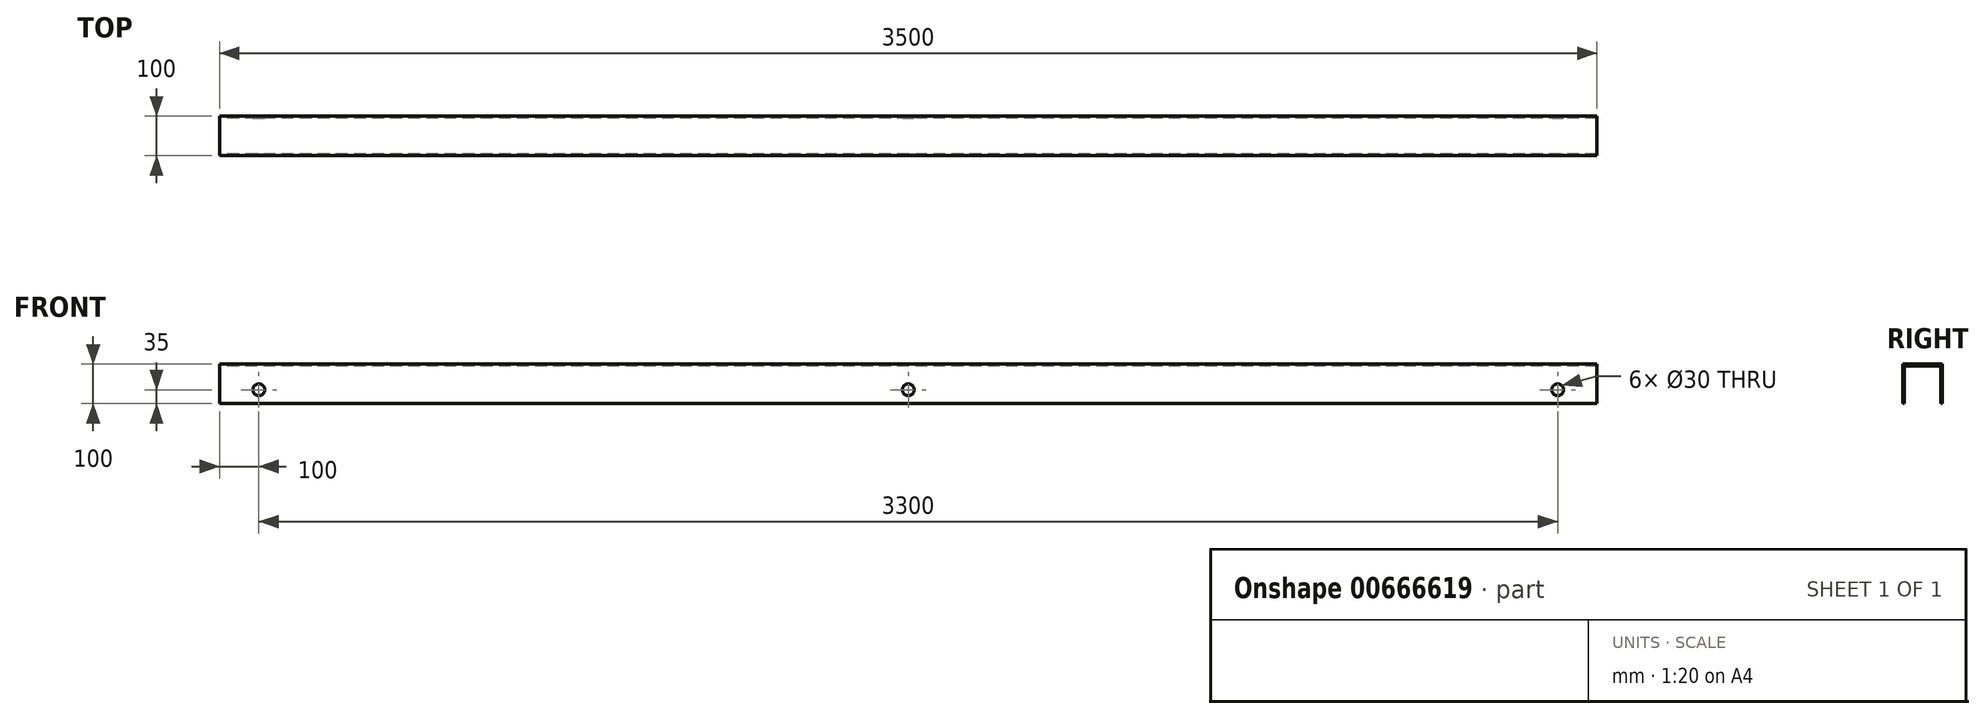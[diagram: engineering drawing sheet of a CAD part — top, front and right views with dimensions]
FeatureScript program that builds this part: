
annotation { "Feature Type Name" : "Feature", "Feature Type Description" : "" }
export const myFeature = defineFeature(function(context is Context, id is Id, definition is map)
    precondition{}
    {
        {
            var Q0;
            Q0=qCreatedBy(makeId("Right.planeOp"),FACE);
            var sketch = newSketch(context, id + "F0", { "sketchPlane" : qUnion([Q0])});
            skLineSegment(sketch, "E0", {"start": v(-37.2, 0) * mm, "end": v(-37.2, 100) * mm});
            skLineSegment(sketch, "E1", {"start": v(-37.2, 100) * mm, "end": v(62.8, 100) * mm});
            skLineSegment(sketch, "E2", {"start": v(62.8, 100) * mm, "end": v(62.8, 0) * mm});
            skLineSegment(sketch, "E3", {"start": v(62.8, 0) * mm, "end": v(58.8, 0) * mm});
            skLineSegment(sketch, "E4", {"start": v(58.8, 0) * mm, "end": v(58.8, 96) * mm});
            skLineSegment(sketch, "E5", {"start": v(58.8, 96) * mm, "end": v(-33.2, 96) * mm});
            skLineSegment(sketch, "E6", {"start": v(-33.2, 96) * mm, "end": v(-33.2, 0) * mm});
            skLineSegment(sketch, "E7", {"start": v(-33.2, 0) * mm, "end": v(-37.2, 0) * mm});
            skSolve(sketch);
        }
        {
            var Q0;
            Q0=makeQuery(id+"F0.imprint","IMPRINT",FACE,{"disambiguationData":[TD([[makeQuery(id+"F0.imprint","IMPRINT",EDGE,{"derivedFrom":sQuery(id+"F0.wireOp",EDGE,"E0")}),-1.0]])]});
            extrude(context, id + "F1", {"entities" : qUnion([Q0]), "depth" : 3500 * mm, "offsetDistance" : 25 * mm});
        }
        {
            var Q0;
            Q0=makeQuery(id+"F1.opExtrude","SWEPT_FACE",FACE,{"disambiguationData":[OSD([sQuery(id+"F0.wireOp",EDGE,"E2")])]});
            var sketch = newSketch(context, id + "F2", { "sketchPlane" : qUnion([Q0])});
            skCircle(sketch, "E8", {"center": v(-3400, 35) * mm, "radius": 15 * mm});
            skCircle(sketch, "E9", {"center": v(-1750, 35) * mm, "radius": 15 * mm});
            skCircle(sketch, "E10", {"center": v(-100, 35) * mm, "radius": 15 * mm});
            skSolve(sketch);
        }
        {
            var Q0;
            Q0=makeQuery(id+"F2.imprint","IMPRINT",FACE,{"disambiguationData":[TD([[makeQuery(id+"F2.imprint","IMPRINT",EDGE,{"derivedFrom":sQuery(id+"F2.wireOp",EDGE,"E8")}),1.0]])]});
            var Q1;
            Q1=makeQuery(id+"F2.imprint","IMPRINT",FACE,{"disambiguationData":[TD([[makeQuery(id+"F2.imprint","IMPRINT",EDGE,{"derivedFrom":sQuery(id+"F2.wireOp",EDGE,"E9")}),1.0]])]});
            var Q2;
            Q2=makeQuery(id+"F2.imprint","IMPRINT",FACE,{"disambiguationData":[TD([[makeQuery(id+"F2.imprint","IMPRINT",EDGE,{"derivedFrom":sQuery(id+"F2.wireOp",EDGE,"E10")}),1.0]])]});
            extrude(context, id + "F3", {"entities" : qUnion([Q0, Q1, Q2]), "operationType" : NewBodyOperationType.REMOVE, "oppositeDirection" : true, "depth" : 4 * mm, "offsetDistance" : 25 * mm});
        }
        {
            var Q0;
            Q0=makeQuery(id+"F1.opExtrude","SWEPT_FACE",FACE,{"disambiguationData":[OSD([sQuery(id+"F0.wireOp",EDGE,"E0")])]});
            var sketch = newSketch(context, id + "F4", { "sketchPlane" : qUnion([Q0])});
            skCircle(sketch, "E11", {"center": v(100, 35) * mm, "radius": 15 * mm});
            skCircle(sketch, "E12", {"center": v(1750, 35) * mm, "radius": 15 * mm});
            skCircle(sketch, "E13", {"center": v(3400, 35) * mm, "radius": 15 * mm});
            skSolve(sketch);
        }
        {
            var Q0;
            Q0=makeQuery(id+"F4.imprint","IMPRINT",FACE,{"disambiguationData":[TD([[makeQuery(id+"F4.imprint","IMPRINT",EDGE,{"derivedFrom":sQuery(id+"F4.wireOp",EDGE,"E11")}),1.0]])]});
            var Q1;
            Q1=makeQuery(id+"F4.imprint","IMPRINT",FACE,{"disambiguationData":[TD([[makeQuery(id+"F4.imprint","IMPRINT",EDGE,{"derivedFrom":sQuery(id+"F4.wireOp",EDGE,"E12")}),1.0]])]});
            var Q2;
            Q2=makeQuery(id+"F4.imprint","IMPRINT",FACE,{"disambiguationData":[TD([[makeQuery(id+"F4.imprint","IMPRINT",EDGE,{"derivedFrom":sQuery(id+"F4.wireOp",EDGE,"E13")}),1.0]])]});
            extrude(context, id + "F5", {"entities" : qUnion([Q0, Q1, Q2]), "operationType" : NewBodyOperationType.REMOVE, "oppositeDirection" : true, "depth" : 5 * mm, "offsetDistance" : 25 * mm});
        }
    });
